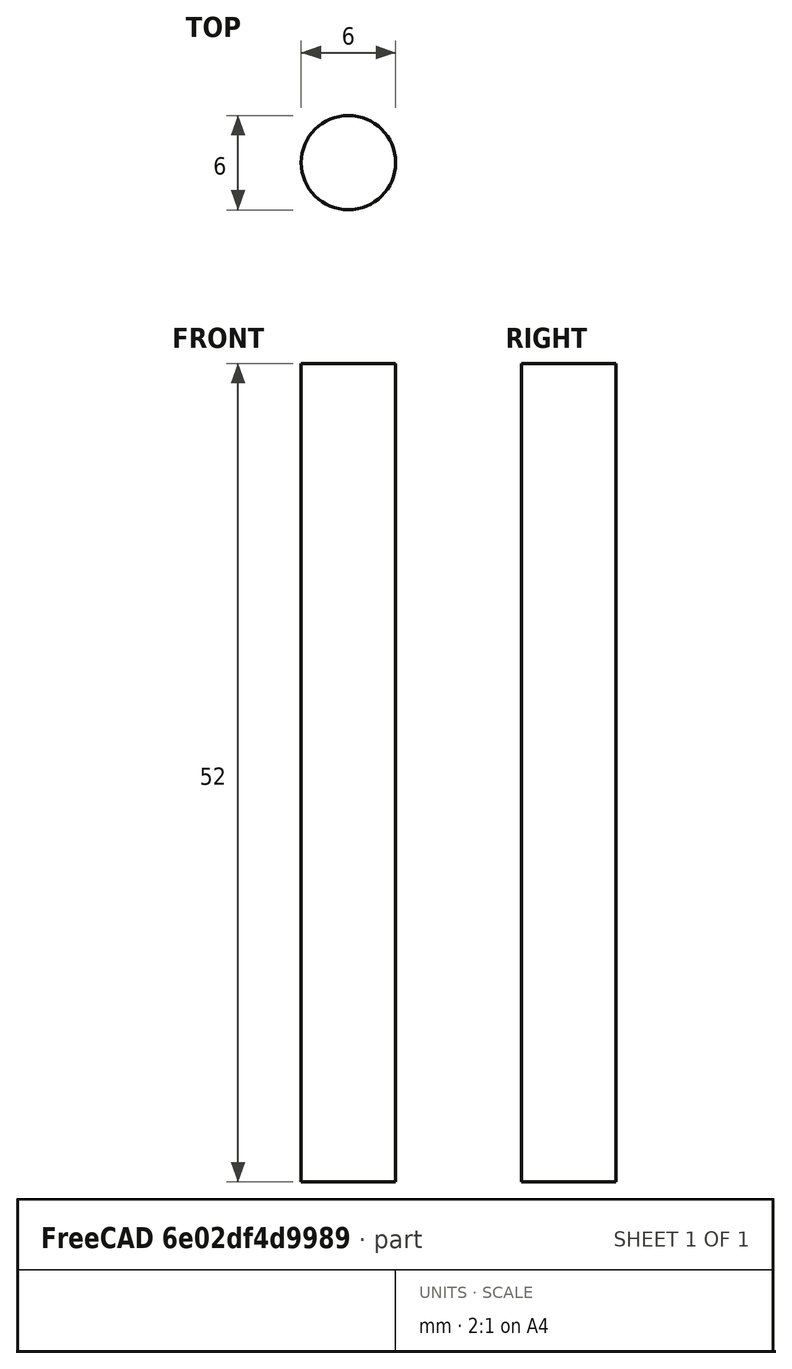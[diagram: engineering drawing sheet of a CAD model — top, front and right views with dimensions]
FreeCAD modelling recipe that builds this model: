
FCSTD DOCUMENT  (FreeCAD 1.0R39319 (Git))
Label: taper pin
License: All rights reserved
LicenseURL: https://en.wikipedia.org/wiki/All_rights_reserved
objects: Sketcher::SketchObject×1, PartDesign::Pad×1, PartDesign::Body×1
note: 6 computed .brp shape members not serialized (recipe doc carries the construction recipe); baked Part::Feature solids carry a one-line shape summary decoded from their .brp

FEATURE [Sketcher::SketchObject] Sketch
  ArcFitTolerance = 1e-06
  AttachmentSupport = -> [XY_Plane]
  FullyConstrained = true
  MakeInternals = false
  MapMode = 5
  sketch-geometry (1):
    g0: Circle CenterX=0 CenterY=0 CenterZ=0 NormalX=0 NormalY=0 NormalZ=1 AngleXU=0 Radius=2.995
  constraints (2):
    c: Coincident(g0,g-1)
    c: Diameter(g0) = 5.99
FEATURE [PartDesign::Pad] Pad
  Direction = (0,0,1)
  Length = 52
  Length2 = 10
  Profile = -> Sketch
  ReferenceAxis = -> Sketch [N_Axis]
  Refine = true
  Suppressed = false
  Type = 0
FEATURE [PartDesign::Body] Body  label="taper pin"
  AllowCompound = false
  Group = -> [Sketch,Pad]
  Origin = -> Origin
  Tip = -> Pad
